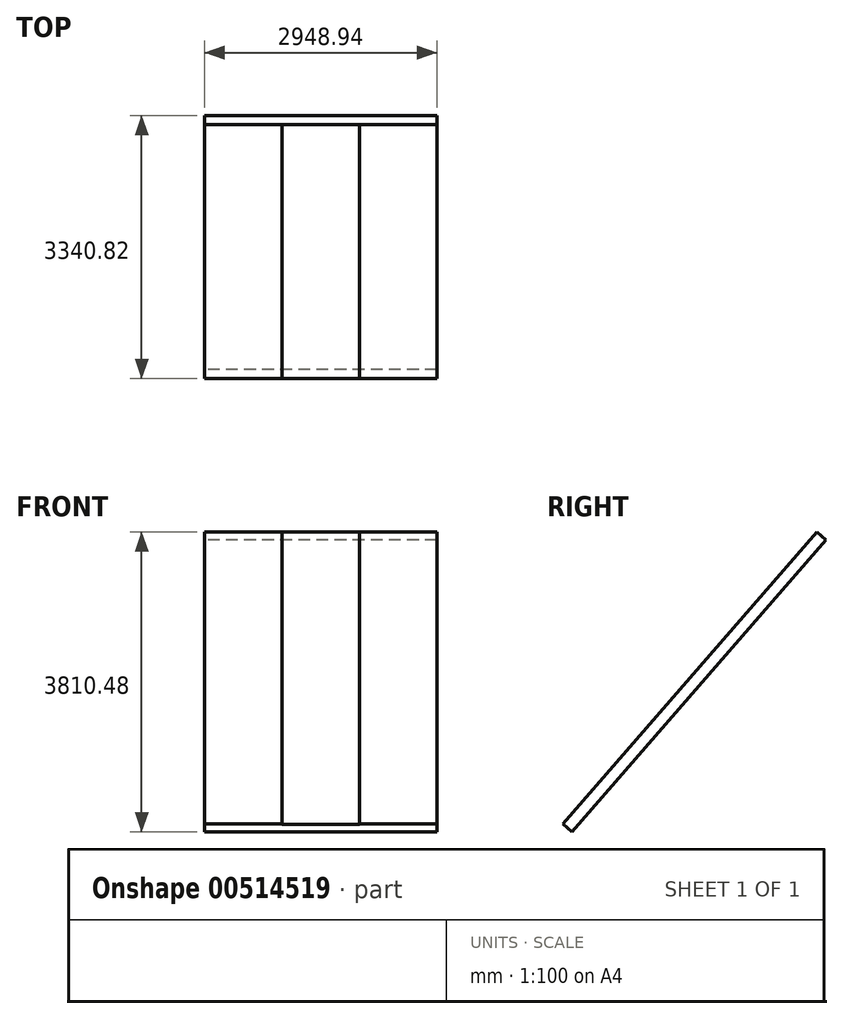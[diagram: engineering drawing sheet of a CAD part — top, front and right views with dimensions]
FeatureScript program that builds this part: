
annotation { "Feature Type Name" : "Feature", "Feature Type Description" : "" }
export const myFeature = defineFeature(function(context is Context, id is Id, definition is map)
    precondition{}
    {
        {
            var Q0;
            Q0=qCreatedBy(makeId("Right.planeOp"),FACE);
            var sketch = newSketch(context, id + "F0", { "sketchPlane" : qUnion([Q0])});
            skLineSegment(sketch, "E0", {"start": v(0, 0) * mm, "end": v(0, 727.93) * mm});
            skLineSegment(sketch, "E1", {"start": v(0, 727.93) * mm, "end": v(288.36, 1059.65) * mm});
            skLineSegment(sketch, "E2", {"start": v(288.36, 1059.65) * mm, "end": v(-2936.1, -2649.68) * mm});
            skLineSegment(sketch, "E3", {"start": v(-2936.1, -2649.68) * mm, "end": v(-3052.46, -2548.53) * mm});
            skLineSegment(sketch, "E4", {"start": v(-3052.46, -2548.53) * mm, "end": v(172, 1160.8) * mm});
            skLineSegment(sketch, "E5", {"start": v(172, 1160.8) * mm, "end": v(288.36, 1059.65) * mm});
            skSolve(sketch);
        }
        {
            var Q0;
            Q0=makeQuery(id+"F0.imprint","IMPRINT",FACE,{"disambiguationData":[TD([[makeQuery(id+"F0.imprint","IMPRINT",EDGE,{"derivedFrom":sQuery(id+"F0.wireOp",EDGE,"E1")}),1.0]])]});
            extrude(context, id + "F1", {"entities" : qUnion([Q0]), "depth" : 2948.94 * mm, "offsetDistance" : 25.4 * mm});
        }
        {
            var Q0;
            Q0=makeQuery(id+"F1.opExtrude","SWEPT_FACE",FACE,{"disambiguationData":[OSD([sQuery(id+"F0.wireOp",EDGE,"E4")])]});
            var sketch = newSketch(context, id + "F2", { "sketchPlane" : qUnion([Q0])});
            skLineSegment(sketch, "E6", {"start": v(0, 988.9) * mm, "end": v(0, -3926) * mm});
            skLineSegment(sketch, "E7", {"start": v(0, -3926) * mm, "end": v(2948.94, -3926) * mm});
            skLineSegment(sketch, "E8", {"start": v(2948.94, -3926) * mm, "end": v(2948.94, 988.9) * mm});
            skLineSegment(sketch, "E9", {"start": v(2948.94, 988.9) * mm, "end": v(0, 988.9) * mm});
            skLineSegment(sketch, "E10", {"start": v(982.98, 988.9) * mm, "end": v(982.98, -3926) * mm});
            skLineSegment(sketch, "E11", {"start": v(1965.96, -3926) * mm, "end": v(1965.96, 988.9) * mm});
            skLineSegment(sketch, "E12", {"start": v(0, -649.4) * mm, "end": v(2948.94, -649.4) * mm});
            skLineSegment(sketch, "E13", {"start": v(0, -2287.7) * mm, "end": v(2948.94, -2287.7) * mm});
            skLineSegment(sketch, "E14.bottom", {"start": v(982.98, 988.9) * mm, "end": v(981.7, 988.9) * mm});
            skLineSegment(sketch, "E14.top", {"start": v(982.98, -3926) * mm, "end": v(981.71, -3926) * mm});
            skLineSegment(sketch, "E14.right", {"start": v(981.7, 988.9) * mm, "end": v(981.71, -3926) * mm});
            skLineSegment(sketch, "E15.bottom", {"start": v(982.98, -3926) * mm, "end": v(984.25, -3926) * mm});
            skLineSegment(sketch, "E15.top", {"start": v(982.98, 988.9) * mm, "end": v(984.25, 988.9) * mm});
            skLineSegment(sketch, "E15.left", {"start": v(982.98, -3926) * mm, "end": v(982.98, 988.9) * mm});
            skLineSegment(sketch, "E15.right", {"start": v(984.25, -3926) * mm, "end": v(984.25, 988.9) * mm});
            skLineSegment(sketch, "E16.bottom", {"start": v(1965.96, 988.9) * mm, "end": v(1967.23, 988.9) * mm});
            skLineSegment(sketch, "E16.top", {"start": v(1965.96, -3926) * mm, "end": v(1967.23, -3926) * mm});
            skLineSegment(sketch, "E16.left", {"start": v(1965.96, 988.9) * mm, "end": v(1965.96, -3926) * mm});
            skLineSegment(sketch, "E16.right", {"start": v(1967.23, 988.9) * mm, "end": v(1967.23, -3926) * mm});
            skLineSegment(sketch, "E17.bottom", {"start": v(1965.96, -3926) * mm, "end": v(1964.7, -3926) * mm});
            skLineSegment(sketch, "E17.top", {"start": v(1965.96, 988.9) * mm, "end": v(1964.69, 988.9) * mm});
            skLineSegment(sketch, "E17.right", {"start": v(1964.7, -3926) * mm, "end": v(1964.69, 988.9) * mm});
            skLineSegment(sketch, "E18.top", {"start": v(0, -648.12) * mm, "end": v(2948.94, -648.12) * mm});
            skLineSegment(sketch, "E18.left", {"start": v(0, -649.4) * mm, "end": v(0, -648.12) * mm});
            skLineSegment(sketch, "E18.right", {"start": v(2948.94, -649.4) * mm, "end": v(2948.94, -648.12) * mm});
            skLineSegment(sketch, "E19.bottom", {"start": v(2948.94, -649.4) * mm, "end": v(0, -649.4) * mm});
            skLineSegment(sketch, "E19.top", {"start": v(2948.94, -650.66) * mm, "end": v(0, -650.66) * mm});
            skLineSegment(sketch, "E19.left", {"start": v(2948.94, -649.4) * mm, "end": v(2948.94, -650.66) * mm});
            skLineSegment(sketch, "E19.right", {"start": v(0, -649.4) * mm, "end": v(0, -650.66) * mm});
            skLineSegment(sketch, "E20.top", {"start": v(0, -2286.42) * mm, "end": v(2948.94, -2286.42) * mm});
            skLineSegment(sketch, "E20.left", {"start": v(0, -2287.7) * mm, "end": v(0, -2286.42) * mm});
            skLineSegment(sketch, "E20.right", {"start": v(2948.94, -2287.7) * mm, "end": v(2948.94, -2286.42) * mm});
            skLineSegment(sketch, "E21.bottom", {"start": v(2948.94, -2287.7) * mm, "end": v(0, -2287.7) * mm});
            skLineSegment(sketch, "E21.top", {"start": v(2948.94, -2288.96) * mm, "end": v(0, -2288.96) * mm});
            skLineSegment(sketch, "E21.left", {"start": v(2948.94, -2287.7) * mm, "end": v(2948.94, -2288.96) * mm});
            skLineSegment(sketch, "E21.right", {"start": v(0, -2287.7) * mm, "end": v(0, -2288.96) * mm});
            skSolve(sketch);
        }
        {
            var Q0;
            {var subQ5=sQuery(id+"F2.wireOp",EDGE,"E18.left");Q0=makeQuery(id+"F2.imprint","IMPRINT",FACE,{"disambiguationData":[TD([[makeQuery(id+"F2.imprint","IMPRINT",EDGE,{"derivedFrom":subQ5}),-1.0]])]});}
            var Q1;
            {var subQ0=sQuery(id+"F2.wireOp",EDGE,"E14.bottom");Q1=makeQuery(id+"F2.imprint","IMPRINT",FACE,{"disambiguationData":[TD([[makeQuery(id+"F2.imprint","IMPRINT",EDGE,{"derivedFrom":subQ0}),1.0]])]});}
            var Q2;
            {var subQ0=sQuery(id+"F2.wireOp",EDGE,"E15.top");Q2=makeQuery(id+"F2.imprint","IMPRINT",FACE,{"disambiguationData":[TD([[makeQuery(id+"F2.imprint","IMPRINT",EDGE,{"derivedFrom":subQ0}),1.0]])]});}
            var Q3;
            {var subQ5=sQuery(id+"F2.wireOp",EDGE,"E19.right");Q3=makeQuery(id+"F2.imprint","IMPRINT",FACE,{"disambiguationData":[TD([[makeQuery(id+"F2.imprint","IMPRINT",EDGE,{"derivedFrom":subQ5}),-1.0]])]});}
            var Q4;
            {var subQ0=sQuery(id+"F2.wireOp",EDGE,"E19.bottom");var subQ1=sQuery(id+"F2.wireOp",EDGE,"E15.right");var subQ2=makeQuery(id+"F2.imprint","INTERSECT",VERTEX,{"derivedFrom":[subQ1,subQ0]});Q4=makeQuery(id+"F2.imprint","IMPRINT",FACE,{"disambiguationData":[TD([[makeQuery(id+"F2.imprint","IMPRINT",EDGE,{"disambiguationData":[TD([[subQ2,-1.0]])],"derivedFrom":subQ1}),-1.0]])]});}
            var Q5;
            {var subQ0=sQuery(id+"F2.wireOp",EDGE,"E19.top");var subQ1=sQuery(id+"F2.wireOp",EDGE,"E15.right");var subQ2=makeQuery(id+"F2.imprint","INTERSECT",VERTEX,{"derivedFrom":[subQ1,subQ0]});Q5=makeQuery(id+"F2.imprint","IMPRINT",FACE,{"disambiguationData":[TD([[makeQuery(id+"F2.imprint","IMPRINT",EDGE,{"disambiguationData":[TD([[subQ2,-1.0]])],"derivedFrom":subQ1}),-1.0]])]});}
            var Q6;
            {var subQ0=sQuery(id+"F2.wireOp",EDGE,"E18.top");var subQ1=sQuery(id+"F2.wireOp",EDGE,"E14.right");var subQ2=makeQuery(id+"F2.imprint","INTERSECT",VERTEX,{"derivedFrom":[subQ1,subQ0]});Q6=makeQuery(id+"F2.imprint","IMPRINT",FACE,{"disambiguationData":[TD([[makeQuery(id+"F2.imprint","IMPRINT",EDGE,{"disambiguationData":[TD([[subQ2,-1.0]])],"derivedFrom":subQ1}),1.0]])]});}
            var Q7;
            {var subQ0=sQuery(id+"F2.wireOp",EDGE,"E19.bottom");var subQ1=sQuery(id+"F2.wireOp",EDGE,"E15.left");var subQ2=makeQuery(id+"F2.imprint","INTERSECT",VERTEX,{"derivedFrom":[subQ1,subQ0]});Q7=makeQuery(id+"F2.imprint","IMPRINT",FACE,{"disambiguationData":[TD([[makeQuery(id+"F2.imprint","IMPRINT",EDGE,{"disambiguationData":[TD([[subQ2,-1.0]])],"derivedFrom":subQ1}),-1.0]])]});}
            var Q8;
            {var subQ0=sQuery(id+"F2.wireOp",EDGE,"E19.bottom");var subQ1=sQuery(id+"F2.wireOp",EDGE,"E14.right");var subQ2=makeQuery(id+"F2.imprint","INTERSECT",VERTEX,{"derivedFrom":[subQ1,subQ0]});Q8=makeQuery(id+"F2.imprint","IMPRINT",FACE,{"disambiguationData":[TD([[makeQuery(id+"F2.imprint","IMPRINT",EDGE,{"disambiguationData":[TD([[subQ2,-1.0]])],"derivedFrom":subQ1}),1.0]])]});}
            var Q9;
            {var subQ0=sQuery(id+"F2.wireOp",EDGE,"E19.top");var subQ1=sQuery(id+"F2.wireOp",EDGE,"E15.left");var subQ2=makeQuery(id+"F2.imprint","INTERSECT",VERTEX,{"derivedFrom":[subQ1,subQ0]});Q9=makeQuery(id+"F2.imprint","IMPRINT",FACE,{"disambiguationData":[TD([[makeQuery(id+"F2.imprint","IMPRINT",EDGE,{"disambiguationData":[TD([[subQ2,-1.0]])],"derivedFrom":subQ1}),-1.0]])]});}
            var Q10;
            {var subQ0=sQuery(id+"F2.wireOp",EDGE,"E20.top");var subQ1=sQuery(id+"F2.wireOp",EDGE,"E15.left");var subQ2=makeQuery(id+"F2.imprint","INTERSECT",VERTEX,{"derivedFrom":[subQ1,subQ0]});Q10=makeQuery(id+"F2.imprint","IMPRINT",FACE,{"disambiguationData":[TD([[makeQuery(id+"F2.imprint","IMPRINT",EDGE,{"disambiguationData":[TD([[subQ2,-1.0]])],"derivedFrom":subQ1}),-1.0]])]});}
            var Q11;
            {var subQ0=sQuery(id+"F2.wireOp",EDGE,"E19.top");var subQ1=sQuery(id+"F2.wireOp",EDGE,"E14.right");var subQ2=makeQuery(id+"F2.imprint","INTERSECT",VERTEX,{"derivedFrom":[subQ1,subQ0]});Q11=makeQuery(id+"F2.imprint","IMPRINT",FACE,{"disambiguationData":[TD([[makeQuery(id+"F2.imprint","IMPRINT",EDGE,{"disambiguationData":[TD([[subQ2,-1.0]])],"derivedFrom":subQ1}),1.0]])]});}
            var Q12;
            {var subQ0=sQuery(id+"F2.wireOp",EDGE,"E16.bottom");Q12=makeQuery(id+"F2.imprint","IMPRINT",FACE,{"disambiguationData":[TD([[makeQuery(id+"F2.imprint","IMPRINT",EDGE,{"derivedFrom":subQ0}),1.0]])]});}
            var Q13;
            {var subQ0=sQuery(id+"F2.wireOp",EDGE,"E17.top");Q13=makeQuery(id+"F2.imprint","IMPRINT",FACE,{"disambiguationData":[TD([[makeQuery(id+"F2.imprint","IMPRINT",EDGE,{"derivedFrom":subQ0}),1.0]])]});}
            var Q14;
            {var subQ0=sQuery(id+"F2.wireOp",EDGE,"E19.bottom");var subQ1=sQuery(id+"F2.wireOp",EDGE,"E11");var subQ2=makeQuery(id+"F2.imprint","INTERSECT",VERTEX,{"derivedFrom":[subQ1,subQ0]});Q14=makeQuery(id+"F2.imprint","IMPRINT",FACE,{"disambiguationData":[TD([[makeQuery(id+"F2.imprint","IMPRINT",EDGE,{"disambiguationData":[TD([[subQ2,-1.0]])],"derivedFrom":subQ1}),1.0]])]});}
            var Q15;
            {var subQ0=sQuery(id+"F2.wireOp",EDGE,"E19.top");var subQ1=sQuery(id+"F2.wireOp",EDGE,"E11");var subQ2=makeQuery(id+"F2.imprint","INTERSECT",VERTEX,{"derivedFrom":[subQ1,subQ0]});Q15=makeQuery(id+"F2.imprint","IMPRINT",FACE,{"disambiguationData":[TD([[makeQuery(id+"F2.imprint","IMPRINT",EDGE,{"disambiguationData":[TD([[subQ2,-1.0]])],"derivedFrom":subQ1}),1.0]])]});}
            var Q16;
            {var subQ0=sQuery(id+"F2.wireOp",EDGE,"E18.top");var subQ1=sQuery(id+"F2.wireOp",EDGE,"E16.right");var subQ2=makeQuery(id+"F2.imprint","INTERSECT",VERTEX,{"derivedFrom":[subQ1,subQ0]});Q16=makeQuery(id+"F2.imprint","IMPRINT",FACE,{"disambiguationData":[TD([[makeQuery(id+"F2.imprint","IMPRINT",EDGE,{"disambiguationData":[TD([[subQ2,-1.0]])],"derivedFrom":subQ1}),-1.0]])]});}
            var Q17;
            {var subQ0=sQuery(id+"F2.wireOp",EDGE,"E19.bottom");var subQ1=sQuery(id+"F2.wireOp",EDGE,"E16.right");var subQ2=makeQuery(id+"F2.imprint","INTERSECT",VERTEX,{"derivedFrom":[subQ1,subQ0]});Q17=makeQuery(id+"F2.imprint","IMPRINT",FACE,{"disambiguationData":[TD([[makeQuery(id+"F2.imprint","IMPRINT",EDGE,{"disambiguationData":[TD([[subQ2,-1.0]])],"derivedFrom":subQ1}),-1.0]])]});}
            var Q18;
            {var subQ0=sQuery(id+"F2.wireOp",EDGE,"E21.top");var subQ1=sQuery(id+"F2.wireOp",EDGE,"E15.left");var subQ2=makeQuery(id+"F2.imprint","INTERSECT",VERTEX,{"derivedFrom":[subQ1,subQ0]});Q18=makeQuery(id+"F2.imprint","IMPRINT",FACE,{"disambiguationData":[TD([[makeQuery(id+"F2.imprint","IMPRINT",EDGE,{"disambiguationData":[TD([[subQ2,-1.0]])],"derivedFrom":subQ1}),-1.0]])]});}
            var Q19;
            {var subQ0=sQuery(id+"F2.wireOp",EDGE,"E21.bottom");var subQ1=sQuery(id+"F2.wireOp",EDGE,"E15.left");var subQ2=makeQuery(id+"F2.imprint","INTERSECT",VERTEX,{"derivedFrom":[subQ1,subQ0]});Q19=makeQuery(id+"F2.imprint","IMPRINT",FACE,{"disambiguationData":[TD([[makeQuery(id+"F2.imprint","IMPRINT",EDGE,{"disambiguationData":[TD([[subQ2,-1.0]])],"derivedFrom":subQ1}),-1.0]])]});}
            var Q20;
            {var subQ0=sQuery(id+"F2.wireOp",EDGE,"E20.top");var subQ1=sQuery(id+"F2.wireOp",EDGE,"E14.right");var subQ2=makeQuery(id+"F2.imprint","INTERSECT",VERTEX,{"derivedFrom":[subQ1,subQ0]});Q20=makeQuery(id+"F2.imprint","IMPRINT",FACE,{"disambiguationData":[TD([[makeQuery(id+"F2.imprint","IMPRINT",EDGE,{"disambiguationData":[TD([[subQ2,-1.0]])],"derivedFrom":subQ1}),1.0]])]});}
            var Q21;
            {var subQ5=sQuery(id+"F2.wireOp",EDGE,"E20.left");Q21=makeQuery(id+"F2.imprint","IMPRINT",FACE,{"disambiguationData":[TD([[makeQuery(id+"F2.imprint","IMPRINT",EDGE,{"derivedFrom":subQ5}),-1.0]])]});}
            extrude(context, id + "F3", {"entities" : qUnion([Q0, Q1, Q2, Q3, Q4, Q5, Q6, Q7, Q8, Q9, Q10, Q11, Q12, Q13, Q14, Q15, Q16, Q17, Q18, Q19, Q20, Q21]), "operationType" : NewBodyOperationType.REMOVE, "oppositeDirection" : true, "depth" : 2.54 * mm, "offsetDistance" : 25.4 * mm});
        }
        {
            var Q0;
            {var subQ5=sQuery(id+"F2.wireOp",EDGE,"E21.right");Q0=makeQuery(id+"F2.imprint","IMPRINT",FACE,{"disambiguationData":[TD([[makeQuery(id+"F2.imprint","IMPRINT",EDGE,{"derivedFrom":subQ5}),-1.0]])]});}
            var Q1;
            {var subQ0=sQuery(id+"F2.wireOp",EDGE,"E15.bottom");Q1=makeQuery(id+"F2.imprint","IMPRINT",FACE,{"disambiguationData":[TD([[makeQuery(id+"F2.imprint","IMPRINT",EDGE,{"derivedFrom":subQ0}),-1.0]])]});}
            var Q2;
            {var subQ0=sQuery(id+"F2.wireOp",EDGE,"E14.top");Q2=makeQuery(id+"F2.imprint","IMPRINT",FACE,{"disambiguationData":[TD([[makeQuery(id+"F2.imprint","IMPRINT",EDGE,{"derivedFrom":subQ0}),-1.0]])]});}
            var Q3;
            {var subQ0=sQuery(id+"F2.wireOp",EDGE,"E21.bottom");var subQ1=sQuery(id+"F2.wireOp",EDGE,"E14.right");var subQ2=makeQuery(id+"F2.imprint","INTERSECT",VERTEX,{"derivedFrom":[subQ1,subQ0]});Q3=makeQuery(id+"F2.imprint","IMPRINT",FACE,{"disambiguationData":[TD([[makeQuery(id+"F2.imprint","IMPRINT",EDGE,{"disambiguationData":[TD([[subQ2,-1.0]])],"derivedFrom":subQ1}),1.0]])]});}
            var Q4;
            {var subQ0=sQuery(id+"F2.wireOp",EDGE,"E21.top");var subQ1=sQuery(id+"F2.wireOp",EDGE,"E15.right");var subQ2=makeQuery(id+"F2.imprint","INTERSECT",VERTEX,{"derivedFrom":[subQ1,subQ0]});Q4=makeQuery(id+"F2.imprint","IMPRINT",FACE,{"disambiguationData":[TD([[makeQuery(id+"F2.imprint","IMPRINT",EDGE,{"disambiguationData":[TD([[subQ2,-1.0]])],"derivedFrom":subQ1}),-1.0]])]});}
            var Q5;
            {var subQ0=sQuery(id+"F2.wireOp",EDGE,"E21.bottom");var subQ1=sQuery(id+"F2.wireOp",EDGE,"E15.right");var subQ2=makeQuery(id+"F2.imprint","INTERSECT",VERTEX,{"derivedFrom":[subQ1,subQ0]});Q5=makeQuery(id+"F2.imprint","IMPRINT",FACE,{"disambiguationData":[TD([[makeQuery(id+"F2.imprint","IMPRINT",EDGE,{"disambiguationData":[TD([[subQ2,-1.0]])],"derivedFrom":subQ1}),-1.0]])]});}
            var Q6;
            {var subQ5=sQuery(id+"F2.wireOp",EDGE,"E18.right");Q6=makeQuery(id+"F2.imprint","IMPRINT",FACE,{"disambiguationData":[TD([[makeQuery(id+"F2.imprint","IMPRINT",EDGE,{"derivedFrom":subQ5}),1.0]])]});}
            var Q7;
            {var subQ5=sQuery(id+"F2.wireOp",EDGE,"E19.left");Q7=makeQuery(id+"F2.imprint","IMPRINT",FACE,{"disambiguationData":[TD([[makeQuery(id+"F2.imprint","IMPRINT",EDGE,{"derivedFrom":subQ5}),1.0]])]});}
            var Q8;
            {var subQ0=sQuery(id+"F2.wireOp",EDGE,"E19.top");var subQ1=sQuery(id+"F2.wireOp",EDGE,"E16.right");var subQ2=makeQuery(id+"F2.imprint","INTERSECT",VERTEX,{"derivedFrom":[subQ1,subQ0]});Q8=makeQuery(id+"F2.imprint","IMPRINT",FACE,{"disambiguationData":[TD([[makeQuery(id+"F2.imprint","IMPRINT",EDGE,{"disambiguationData":[TD([[subQ2,-1.0]])],"derivedFrom":subQ1}),-1.0]])]});}
            var Q9;
            {var subQ0=sQuery(id+"F2.wireOp",EDGE,"E20.top");var subQ1=sQuery(id+"F2.wireOp",EDGE,"E11");var subQ2=makeQuery(id+"F2.imprint","INTERSECT",VERTEX,{"derivedFrom":[subQ1,subQ0]});Q9=makeQuery(id+"F2.imprint","IMPRINT",FACE,{"disambiguationData":[TD([[makeQuery(id+"F2.imprint","IMPRINT",EDGE,{"disambiguationData":[TD([[subQ2,-1.0]])],"derivedFrom":subQ1}),1.0]])]});}
            var Q10;
            {var subQ0=sQuery(id+"F2.wireOp",EDGE,"E21.bottom");var subQ1=sQuery(id+"F2.wireOp",EDGE,"E11");var subQ2=makeQuery(id+"F2.imprint","INTERSECT",VERTEX,{"derivedFrom":[subQ1,subQ0]});Q10=makeQuery(id+"F2.imprint","IMPRINT",FACE,{"disambiguationData":[TD([[makeQuery(id+"F2.imprint","IMPRINT",EDGE,{"disambiguationData":[TD([[subQ2,-1.0]])],"derivedFrom":subQ1}),1.0]])]});}
            var Q11;
            {var subQ0=sQuery(id+"F2.wireOp",EDGE,"E21.top");var subQ1=sQuery(id+"F2.wireOp",EDGE,"E11");var subQ2=makeQuery(id+"F2.imprint","INTERSECT",VERTEX,{"derivedFrom":[subQ1,subQ0]});Q11=makeQuery(id+"F2.imprint","IMPRINT",FACE,{"disambiguationData":[TD([[makeQuery(id+"F2.imprint","IMPRINT",EDGE,{"disambiguationData":[TD([[subQ2,-1.0]])],"derivedFrom":subQ1}),1.0]])]});}
            var Q12;
            {var subQ0=sQuery(id+"F2.wireOp",EDGE,"E20.top");var subQ1=sQuery(id+"F2.wireOp",EDGE,"E16.right");var subQ2=makeQuery(id+"F2.imprint","INTERSECT",VERTEX,{"derivedFrom":[subQ1,subQ0]});Q12=makeQuery(id+"F2.imprint","IMPRINT",FACE,{"disambiguationData":[TD([[makeQuery(id+"F2.imprint","IMPRINT",EDGE,{"disambiguationData":[TD([[subQ2,-1.0]])],"derivedFrom":subQ1}),-1.0]])]});}
            var Q13;
            {var subQ0=sQuery(id+"F2.wireOp",EDGE,"E21.bottom");var subQ1=sQuery(id+"F2.wireOp",EDGE,"E16.right");var subQ2=makeQuery(id+"F2.imprint","INTERSECT",VERTEX,{"derivedFrom":[subQ1,subQ0]});Q13=makeQuery(id+"F2.imprint","IMPRINT",FACE,{"disambiguationData":[TD([[makeQuery(id+"F2.imprint","IMPRINT",EDGE,{"disambiguationData":[TD([[subQ2,-1.0]])],"derivedFrom":subQ1}),-1.0]])]});}
            var Q14;
            {var subQ5=sQuery(id+"F2.wireOp",EDGE,"E20.right");Q14=makeQuery(id+"F2.imprint","IMPRINT",FACE,{"disambiguationData":[TD([[makeQuery(id+"F2.imprint","IMPRINT",EDGE,{"derivedFrom":subQ5}),1.0]])]});}
            var Q15;
            {var subQ0=sQuery(id+"F2.wireOp",EDGE,"E17.bottom");Q15=makeQuery(id+"F2.imprint","IMPRINT",FACE,{"disambiguationData":[TD([[makeQuery(id+"F2.imprint","IMPRINT",EDGE,{"derivedFrom":subQ0}),-1.0]])]});}
            var Q16;
            {var subQ0=sQuery(id+"F2.wireOp",EDGE,"E16.top");Q16=makeQuery(id+"F2.imprint","IMPRINT",FACE,{"disambiguationData":[TD([[makeQuery(id+"F2.imprint","IMPRINT",EDGE,{"derivedFrom":subQ0}),-1.0]])]});}
            var Q17;
            {var subQ5=sQuery(id+"F2.wireOp",EDGE,"E21.left");Q17=makeQuery(id+"F2.imprint","IMPRINT",FACE,{"disambiguationData":[TD([[makeQuery(id+"F2.imprint","IMPRINT",EDGE,{"derivedFrom":subQ5}),1.0]])]});}
            extrude(context, id + "F4", {"entities" : qUnion([Q0, Q1, Q2, Q3, Q4, Q5, Q6, Q7, Q8, Q9, Q10, Q11, Q12, Q13, Q14, Q15, Q16, Q17]), "operationType" : NewBodyOperationType.REMOVE, "oppositeDirection" : true, "depth" : 2.54 * mm, "offsetDistance" : 25.4 * mm});
        }
    });
